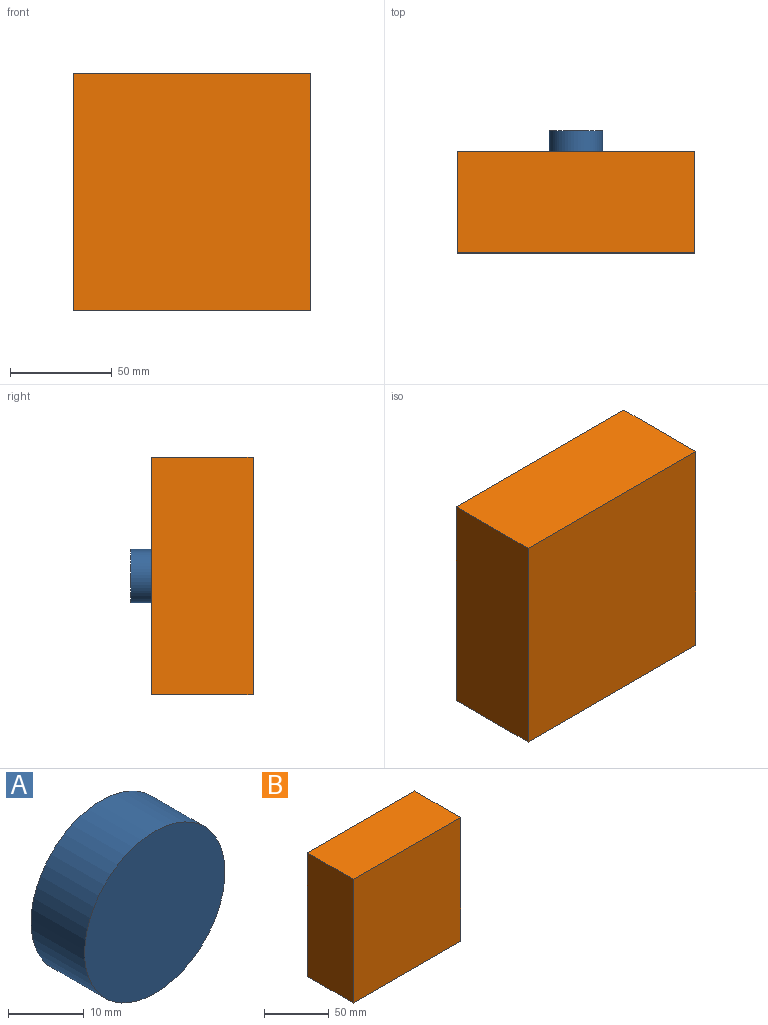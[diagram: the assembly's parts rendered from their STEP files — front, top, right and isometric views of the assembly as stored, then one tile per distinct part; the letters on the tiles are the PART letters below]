
ASSEMBLY  parts=2 mates=1
PART A: 3 faces, bbox 26.2x10x26.2 mm
  f0: cylinder r=13.1mm len=26.19mm, axis (0,1,0), area 822.9mm2, adj f1,f2
  f1: plane 26.19x26.19mm, normal (0,-1,0), area 538.9mm2, adj f0
  f2: plane 26.19x26.19mm, normal (0,1,0), area 538.9mm2, adj f0
PART B: 8 faces, bbox 116.6x50x116.6 mm
  f0: plane 116.55x50mm, normal (0,0,-1), area 5827.7mm2, adj f1,f3,f4,f5
  f1: plane 116.55x50mm, normal (1,0,0), area 5023.5mm2, adj f0,f2,f4,f5,f6
  f2: plane 116.55x50mm, normal (0,0,1), area 5827.7mm2, adj f1,f3,f4,f5
  f3: plane 116.55x50mm, normal (-1,0,0), area 5827.7mm2, adj f0,f2,f4,f5
  f4: plane 116.55x116.55mm, normal (0,-1,0), area 13584.9mm2, adj f0,f1,f2,f3
  f5: plane 116.55x116.55mm, normal (0,1,0), area 13584.9mm2, adj f0,f1,f2,f3
  f6: cylinder r=16mm len=32mm, axis (1,0,0), area 2513.3mm2, adj f1,f7
  f7: plane 32x32mm, normal (1,0,0), area 804.2mm2, adj f6
PLACE A rot(axis=(0,0,1),180deg) t=(-59.06,8.97,-74.91)mm
PLACE B t=(-1.94,8.97,-29.91)mm
MATE planar A.f0 <-> B.f5  axis (0,-1,0) through (-1.94,8.97,-29.91)mm
